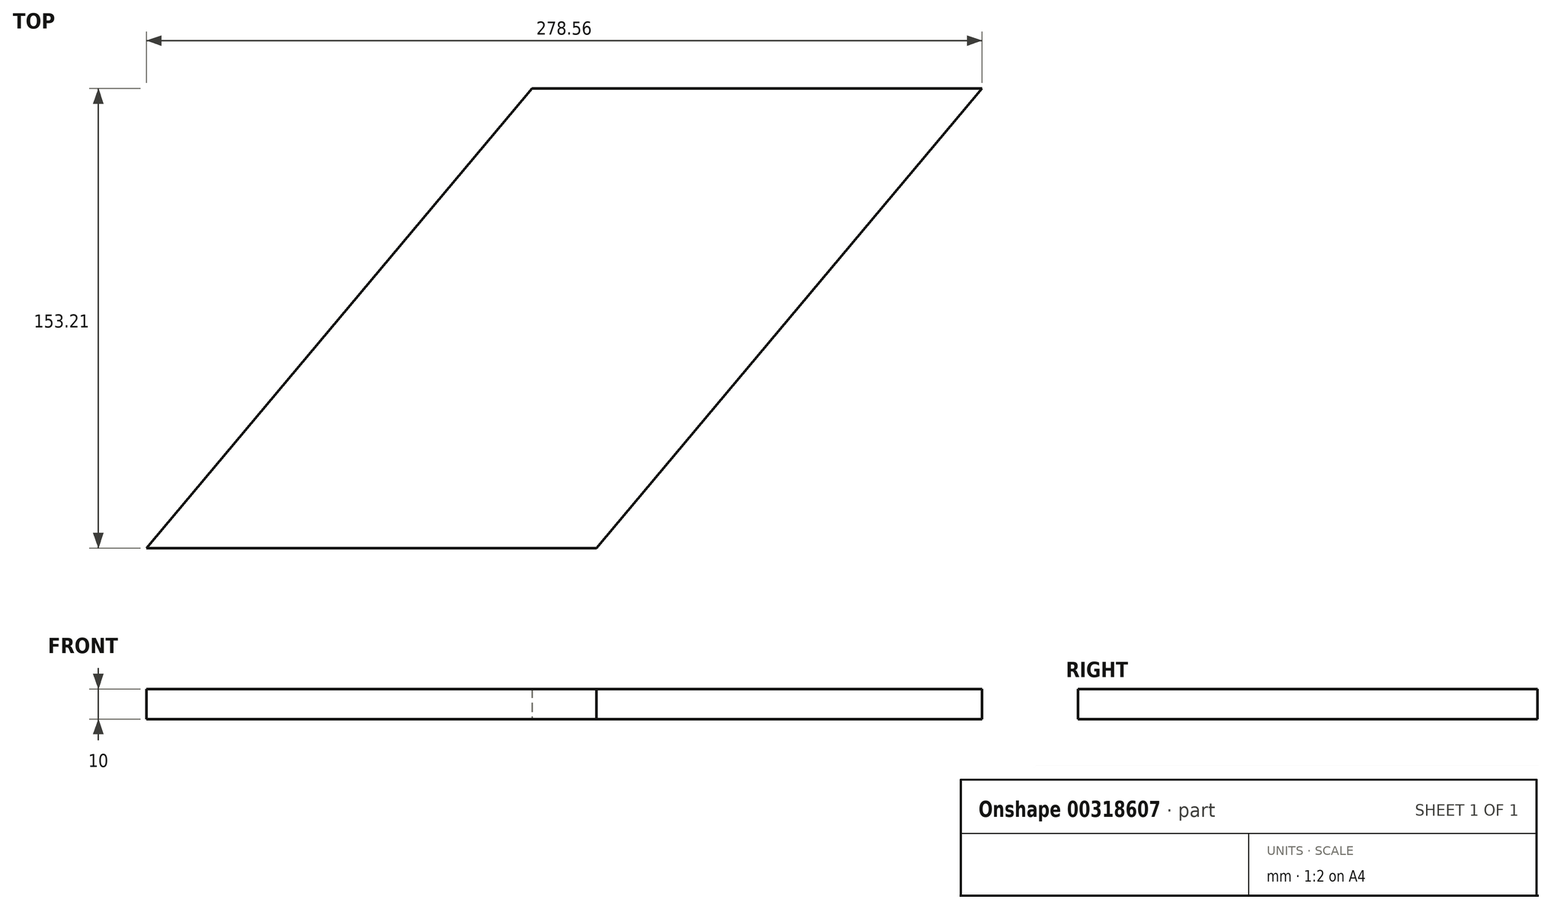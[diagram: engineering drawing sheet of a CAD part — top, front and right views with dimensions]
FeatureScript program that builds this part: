
annotation { "Feature Type Name" : "Feature", "Feature Type Description" : "" }
export const myFeature = defineFeature(function(context is Context, id is Id, definition is map)
    precondition{}
    {
        {
            var Q0;
            Q0=qCreatedBy(makeId("Top.planeOp"),FACE);
            var sketch = newSketch(context, id + "F0", { "sketchPlane" : qUnion([Q0])});
            skLineSegment(sketch, "E0", {"start": v(0, 0) * mm, "end": v(150, 0) * mm});
            skLineSegment(sketch, "E1", {"start": v(150, 0) * mm, "end": v(278.56, 153.2) * mm});
            skLineSegment(sketch, "E2", {"start": v(278.56, 153.2) * mm, "end": v(128.56, 153.2) * mm});
            skLineSegment(sketch, "E3", {"start": v(128.56, 153.2) * mm, "end": v(0, 0) * mm});
            skSolve(sketch);
        }
        {
            var Q0;
            Q0 = qSketchRegion(id + "F0", true);
            extrude(context, id + "F1", {"entities" : qUnion([Q0]), "depth" : 10 * mm});
        }
    });
